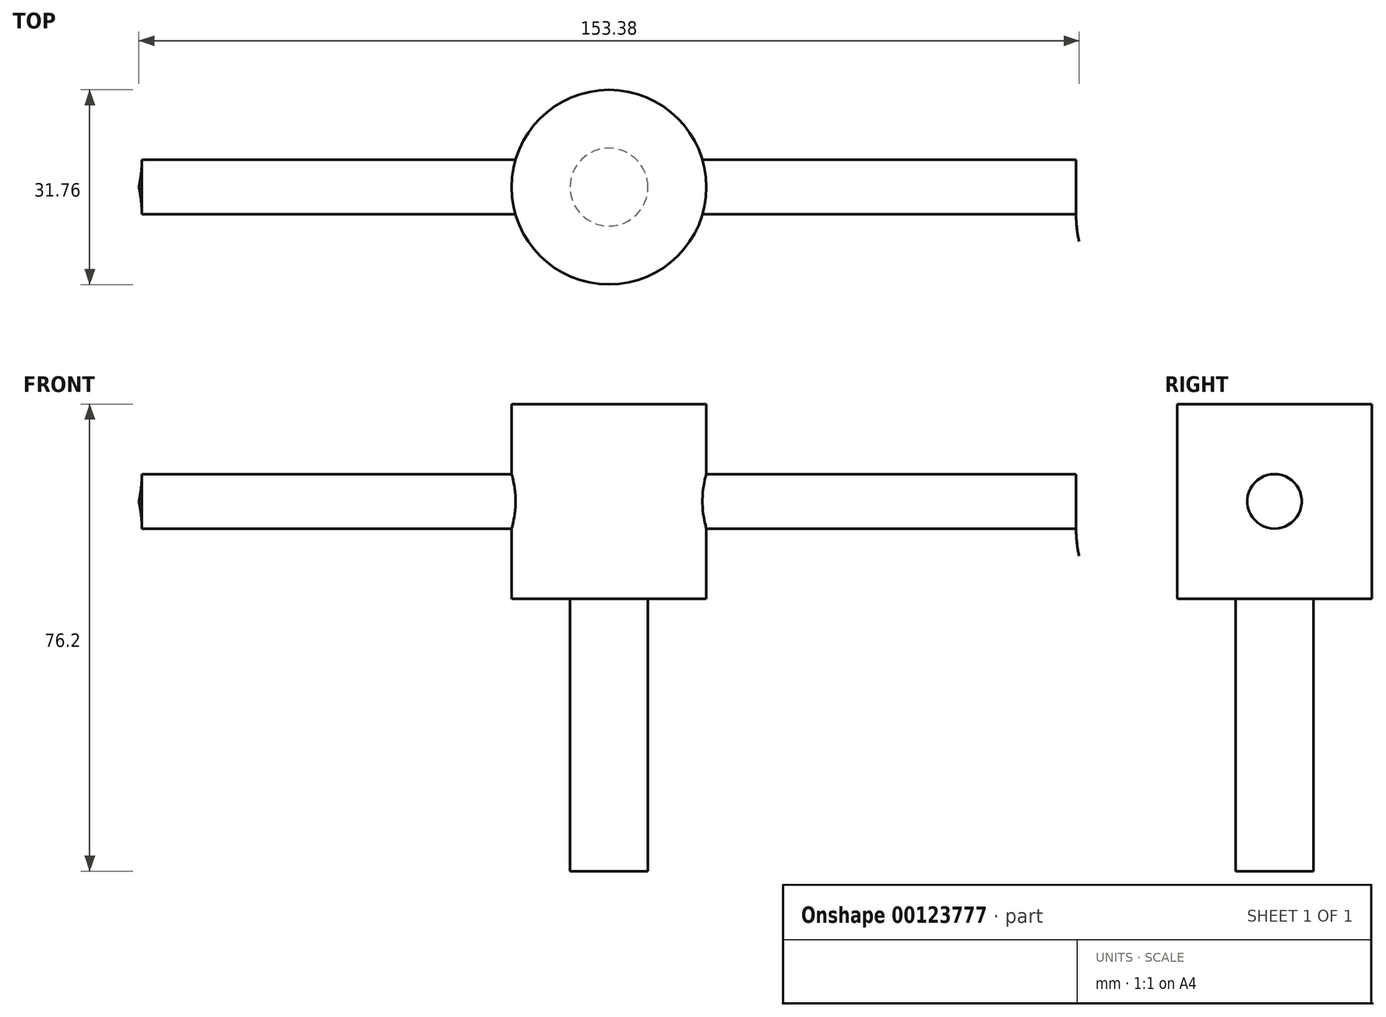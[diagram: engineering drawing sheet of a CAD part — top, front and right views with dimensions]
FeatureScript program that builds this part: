
annotation { "Feature Type Name" : "Feature", "Feature Type Description" : "" }
export const myFeature = defineFeature(function(context is Context, id is Id, definition is map)
    precondition{}
    {
        {
            var Q0;
            Q0=qCreatedBy(makeId("Top.planeOp"),FACE);
            var sketch = newSketch(context, id + "F0", { "sketchPlane" : qUnion([Q0])});
            skCircle(sketch, "E0", {"center": v(0, 0) * mm, "radius": 15.88 * mm});
            skSolve(sketch);
        }
        {
            var Q0;
            Q0=makeQuery(id+"F0.imprint","IMPRINT",FACE,{"disambiguationData":[TD([[makeQuery(id+"F0.imprint","IMPRINT",EDGE,{"derivedFrom":sQuery(id+"F0.wireOp",EDGE,"E0")}),1.0]])]});
            extrude(context, id + "F1", {"entities" : qUnion([Q0]), "oppositeDirection" : true, "depth" : 31.75 * mm});
        }
        {
            var Q0;
            Q0=qCreatedBy(makeId("Top.planeOp"),FACE);
            cPlane(context, id + "F2", {"entities" : qUnion([Q0]), "cplaneType" : CPlaneType.OFFSET, "offset" : 76.2 * mm, "oppositeDirection" : true, "width" : 152.4 * mm, "height" : 152.4 * mm});
        }
        {
            var Q0;
            Q0=qCreatedBy(id+"F2.planeOp",FACE);
            var sketch = newSketch(context, id + "F3", { "sketchPlane" : qUnion([Q0])});
            skCircle(sketch, "E1", {"center": v(0, 0) * mm, "radius": 6.35 * mm});
            skSolve(sketch);
        }
        {
            var Q0;
            Q0 = qSketchRegion(id + "F3", true);
            extrude(context, id + "F4", {"entities" : qUnion([Q0]), "operationType" : NewBodyOperationType.ADD, "depth" : 44.45 * mm});
        }
        {
            var Q0;
            Q0=qCreatedBy(makeId("Right.planeOp"),FACE);
            cPlane(context, id + "F5", {"entities" : qUnion([Q0]), "cplaneType" : CPlaneType.OFFSET, "offset" : 76.2 * mm, "width" : 152.4 * mm, "height" : 152.4 * mm});
        }
        {
            var Q0;
            Q0=qCreatedBy(id+"F5.planeOp",FACE);
            var sketch = newSketch(context, id + "F6", { "sketchPlane" : qUnion([Q0])});
            skLineSegment(sketch, "E2", {"start": v(-15.46, 0) * mm, "end": v(16.3, 0) * mm, "construction": true});
            skLineSegment(sketch, "E3", {"start": v(16.3, 0) * mm, "end": v(16.3, -31.75) * mm, "construction": true});
            skLineSegment(sketch, "E4", {"start": v(16.3, -31.75) * mm, "end": v(-15.46, -31.75) * mm});
            skLineSegment(sketch, "E5", {"start": v(-15.46, -31.75) * mm, "end": v(-15.46, 0) * mm, "construction": true});
            skCircle(sketch, "E6", {"center": v(0, -15.88) * mm, "radius": 4.45 * mm});
            skPoint(sketch, "E6.centerSnap0", {"position": v(16.3, -15.88) * mm});
            skSolve(sketch);
        }
        {
            var Q0;
            Q0=makeQuery(id+"F6.imprint","IMPRINT",FACE,{"disambiguationData":[TD([[makeQuery(id+"F6.imprint","IMPRINT",EDGE,{"derivedFrom":sQuery(id+"F6.wireOp",EDGE,"E6")}),1.0]])]});
            extrude(context, id + "F7", {"entities" : qUnion([Q0]), "operationType" : NewBodyOperationType.ADD, "oppositeDirection" : true, "depth" : 76.2 * mm});
        }
        {
            var Q0;
            Q0=qCreatedBy(id+"F5.planeOp",FACE);
            cPlane(context, id + "F8", {"entities" : qUnion([Q0]), "cplaneType" : CPlaneType.OFFSET, "offset" : 152.4 * mm, "oppositeDirection" : true, "width" : 152.4 * mm, "height" : 152.4 * mm});
        }
        {
            var Q0;
            Q0=qCreatedBy(id+"F8.planeOp",FACE);
            var sketch = newSketch(context, id + "F9", { "sketchPlane" : qUnion([Q0])});
            skLineSegment(sketch, "E7", {"start": v(16.55, 0) * mm, "end": v(-15.2, 0) * mm, "construction": true});
            skLineSegment(sketch, "E8", {"start": v(-15.2, 0) * mm, "end": v(-15.2, -31.75) * mm, "construction": true});
            skLineSegment(sketch, "E9", {"start": v(-15.2, -31.75) * mm, "end": v(16.55, -31.75) * mm, "construction": true});
            skLineSegment(sketch, "E10", {"start": v(16.55, -31.75) * mm, "end": v(16.55, 0) * mm, "construction": true});
            skCircle(sketch, "E11", {"center": v(0, -15.88) * mm, "radius": 4.45 * mm});
            skSolve(sketch);
        }
        {
            var Q0;
            Q0=makeQuery(id+"F9.imprint","IMPRINT",FACE,{"disambiguationData":[TD([[makeQuery(id+"F9.imprint","IMPRINT",EDGE,{"derivedFrom":sQuery(id+"F9.wireOp",EDGE,"E11")}),1.0]])]});
            extrude(context, id + "F10", {"entities" : qUnion([Q0]), "operationType" : NewBodyOperationType.ADD, "depth" : 76.2 * mm});
        }
        {
            var Q0;
            Q0=qCreatedBy(makeId("Front.planeOp"),FACE);
            var sketch = newSketch(context, id + "F11", { "sketchPlane" : qUnion([Q0])});
            skLineSegment(sketch, "E12", {"start": v(0, -15.88) * mm, "end": v(-137.05, -15.88) * mm, "construction": true});
            skLineSegment(sketch, "E13", {"start": v(-76.2, -15.88) * mm, "end": v(-76.2, -11.43) * mm});
            skArc(sketch, "E14", {"start": v(-76.2, -11.43) * mm, "mid": v(-98.76, 8.77) * mm, "end": v(-116.35, -15.88) * mm});
            skLineSegment(sketch, "E15", {"start": v(-116.35, -15.88) * mm, "end": v(-76.2, -15.88) * mm});
            skLineSegment(sketch, "E16", {"start": v(76.2, -15.87) * mm, "end": v(76.2, -11.43) * mm});
            skLineSegment(sketch, "E17", {"start": v(0, -15.87) * mm, "end": v(127.9, -15.87) * mm, "construction": true});
            skArc(sketch, "E18", {"start": v(116.35, -15.87) * mm, "mid": v(98.76, 8.77) * mm, "end": v(76.2, -11.43) * mm});
            skLineSegment(sketch, "E19", {"start": v(76.2, -15.87) * mm, "end": v(116.35, -15.87) * mm});
            skSolve(sketch);
        }
        {
            var Q0;
            Q0=makeQuery(id+"F11.imprint","IMPRINT",FACE,{"disambiguationData":[TD([[makeQuery(id+"F11.imprint","IMPRINT",EDGE,{"derivedFrom":sQuery(id+"F11.wireOp",EDGE,"E13")}),1.0]])]});
            var Q1;
            Q1=sQuery(id+"F11.wireOp",EDGE,"E12");
            revolve(context, id + "F12", {"operationType" : NewBodyOperationType.ADD, "entities" : qUnion([Q0]), "axis" : qUnion([Q1]), "revolveType" : RevolveType.FULL});
        }
        {
            var Q0;
            Q0=makeQuery(id+"F11.imprint","IMPRINT",FACE,{"disambiguationData":[TD([[makeQuery(id+"F11.imprint","IMPRINT",EDGE,{"derivedFrom":sQuery(id+"F11.wireOp",EDGE,"E16")}),-1.0]])]});
            var Q1;
            Q1=sQuery(id+"F11.wireOp",EDGE,"E12");
            revolve(context, id + "F13", {"operationType" : NewBodyOperationType.ADD, "entities" : qUnion([Q0]), "axis" : qUnion([Q1]), "revolveType" : RevolveType.FULL});
        }
    });
